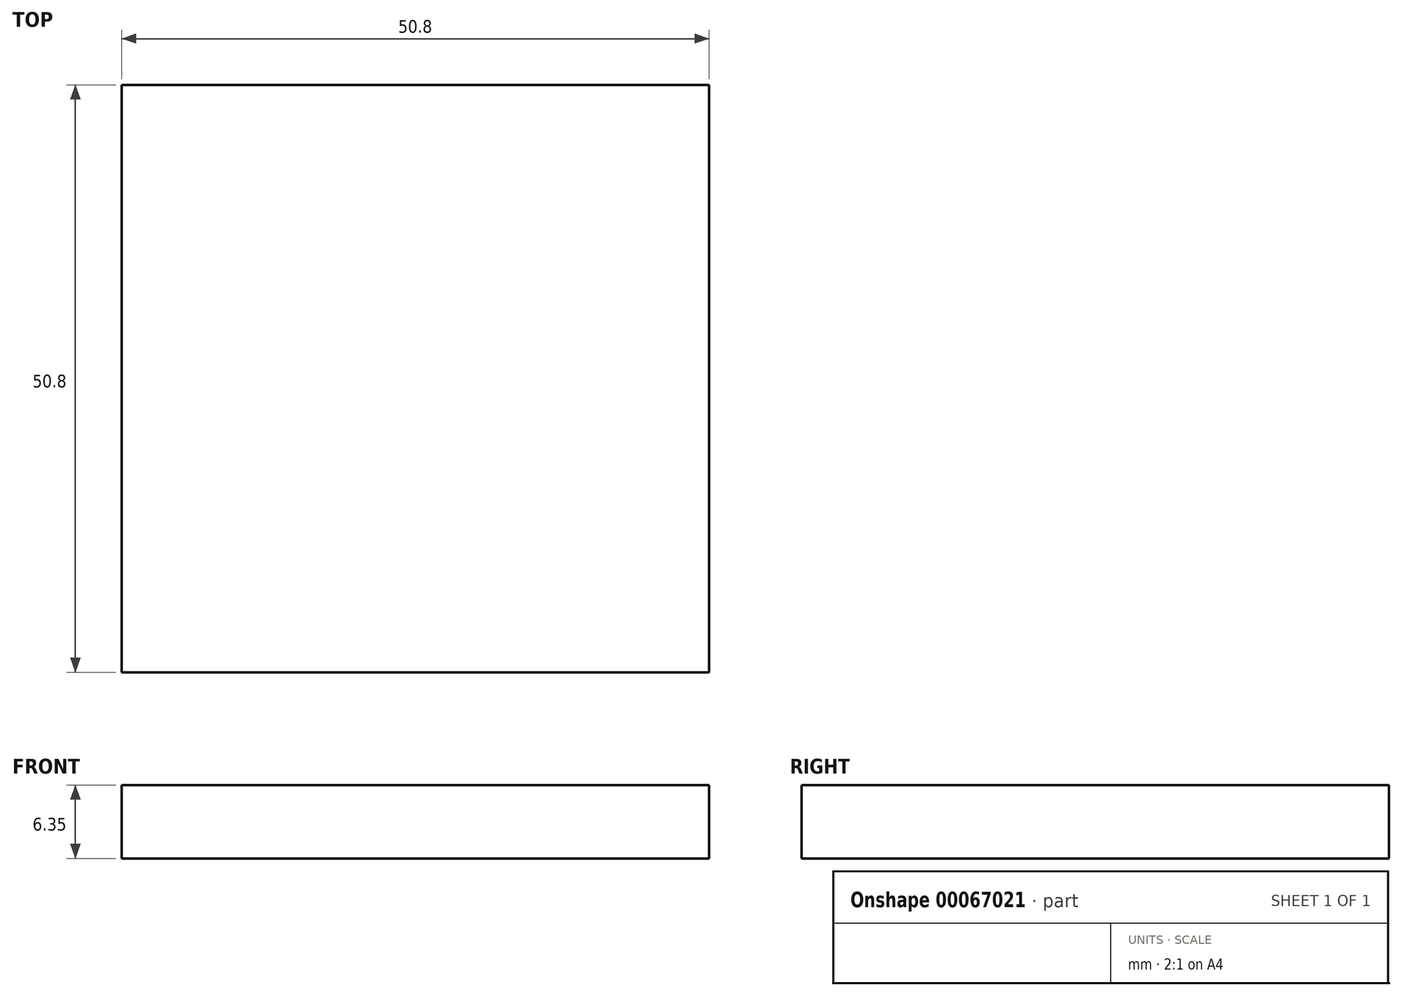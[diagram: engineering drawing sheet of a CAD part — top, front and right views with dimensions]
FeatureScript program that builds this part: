
annotation { "Feature Type Name" : "Feature", "Feature Type Description" : "" }
export const myFeature = defineFeature(function(context is Context, id is Id, definition is map)
    precondition{}
    {
        {
            var Q0;
            Q0=qCreatedBy(makeId("Top.planeOp"),FACE);
            var sketch = newSketch(context, id + "F0", { "sketchPlane" : qUnion([Q0])});
            skLineSegment(sketch, "E0.rect.bottom", {"start": v(25.4, 25.4) * mm, "end": v(-25.4, 25.4) * mm});
            skLineSegment(sketch, "E0.rect.top", {"start": v(25.4, -25.4) * mm, "end": v(-25.4, -25.4) * mm});
            skLineSegment(sketch, "E0.rect.left", {"start": v(25.4, 25.4) * mm, "end": v(25.4, -25.4) * mm});
            skLineSegment(sketch, "E0.rect.right", {"start": v(-25.4, 25.4) * mm, "end": v(-25.4, -25.4) * mm});
            skPoint(sketch, "E0.rect.middle", {"position": v(0, 0) * mm});
            skSolve(sketch);
        }
        {
            var Q0;
            Q0=makeQuery(id+"F0.imprint","IMPRINT",FACE,{"disambiguationData":[TD([[makeQuery(id+"F0.imprint","IMPRINT",EDGE,{"derivedFrom":sQuery(id+"F0.wireOp",EDGE,"E0.rect.bottom")}),1.0]])]});
            extrude(context, id + "F1", {"entities" : qUnion([Q0]), "depth" : 6.35 * mm});
        }
    });
